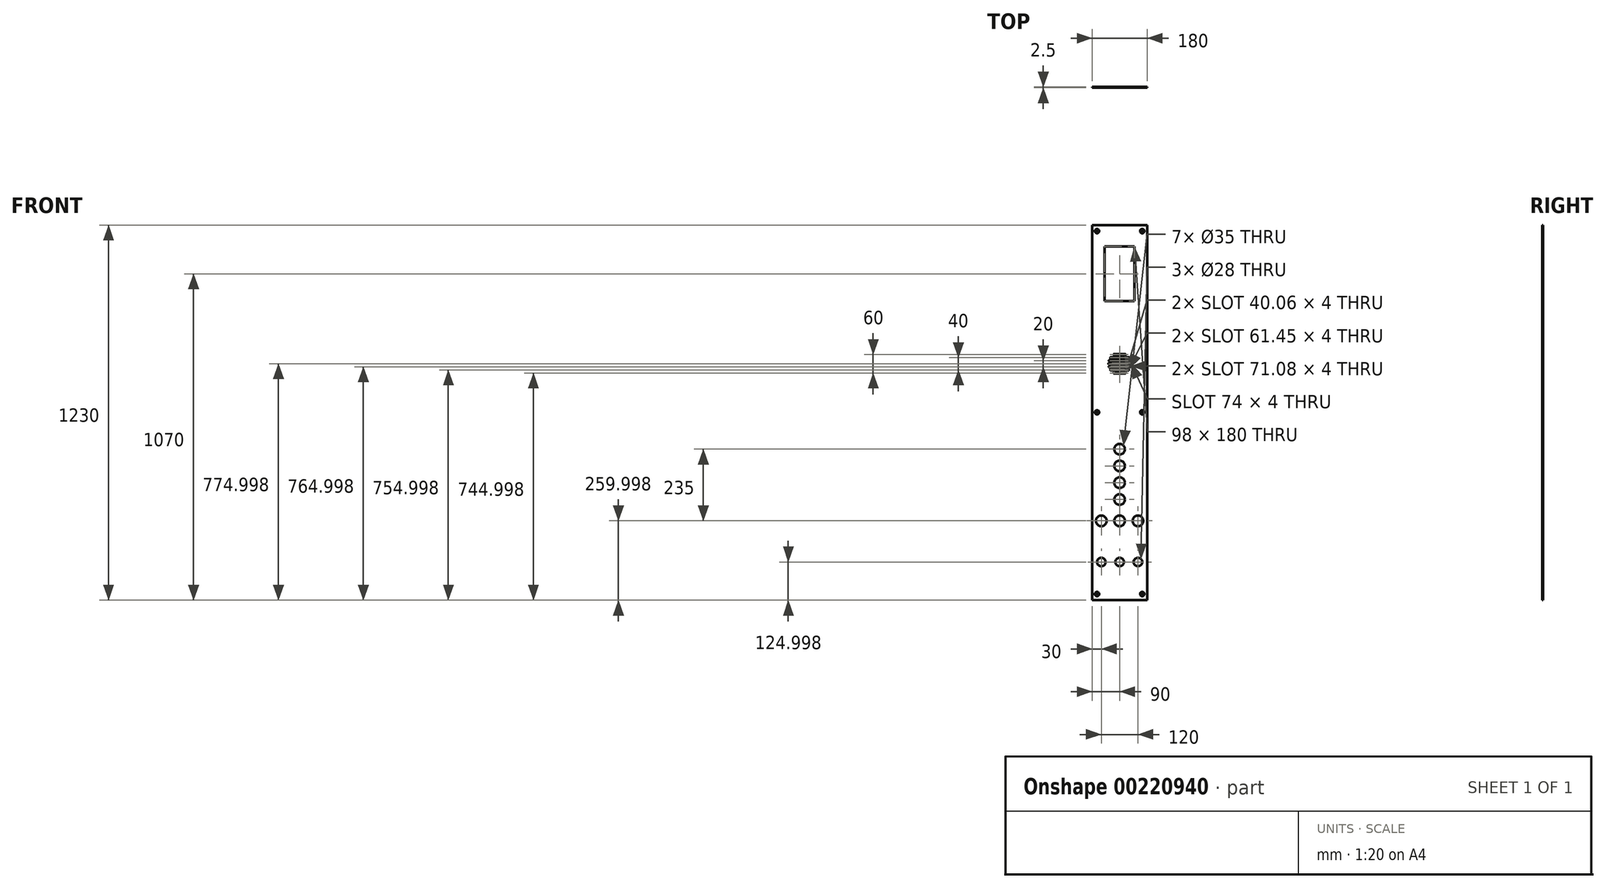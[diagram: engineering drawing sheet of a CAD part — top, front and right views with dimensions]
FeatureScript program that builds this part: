
annotation { "Feature Type Name" : "Feature", "Feature Type Description" : "" }
export const myFeature = defineFeature(function(context is Context, id is Id, definition is map)
    precondition{}
    {
        {
            var Q0;
            Q0=qCreatedBy(makeId("Front.planeOp"),FACE);
            var sketch = newSketch(context, id + "F0", { "sketchPlane" : qUnion([Q0])});
            skLineSegment(sketch, "E0.bottom", {"start": v(-139, 614.56) * mm, "end": v(41, 614.56) * mm});
            skLineSegment(sketch, "E0.top", {"start": v(-139, -615.44) * mm, "end": v(41, -615.44) * mm});
            skLineSegment(sketch, "E0.left", {"start": v(-139, 614.56) * mm, "end": v(-139, -615.44) * mm});
            skLineSegment(sketch, "E0.right", {"start": v(41, 614.56) * mm, "end": v(41, -615.44) * mm});
            skLineSegment(sketch, "E1.bottom", {"start": v(-98, 544.56) * mm, "end": v(0, 544.56) * mm});
            skLineSegment(sketch, "E1.top", {"start": v(-98, 364.56) * mm, "end": v(0, 364.56) * mm});
            skLineSegment(sketch, "E1.left", {"start": v(-98, 544.56) * mm, "end": v(-98, 364.56) * mm});
            skLineSegment(sketch, "E1.right", {"start": v(0, 544.56) * mm, "end": v(0, 364.56) * mm});
            skLineSegment(sketch, "E2", {"start": v(-49, 614.56) * mm, "end": v(-49, -615.44) * mm, "construction": true});
            skCircle(sketch, "E3", {"center": v(-49, -355.44) * mm, "radius": 17.5 * mm});
            skCircle(sketch, "E4", {"center": v(-49, -285.44) * mm, "radius": 17.5 * mm});
            skCircle(sketch, "E5", {"center": v(-49, -230.44) * mm, "radius": 17.5 * mm});
            skCircle(sketch, "E6", {"center": v(-49, -175.44) * mm, "radius": 17.5 * mm});
            skCircle(sketch, "E7", {"center": v(-49, -120.44) * mm, "radius": 17.5 * mm});
            skLineSegment(sketch, "E8", {"start": v(-49, -355.44) * mm, "end": v(-139, -355.44) * mm, "construction": true});
            skLineSegment(sketch, "E9", {"start": v(-49, -355.44) * mm, "end": v(41, -355.44) * mm, "construction": true});
            skCircle(sketch, "E10", {"center": v(-109, -355.44) * mm, "radius": 17.5 * mm});
            skCircle(sketch, "E11", {"center": v(11, -355.44) * mm, "radius": 17.5 * mm});
            skCircle(sketch, "E12", {"center": v(-49, 159.56) * mm, "radius": 35 * mm, "construction": true});
            skLineSegment(sketch, "E13", {"start": v(-84, 159.56) * mm, "end": v(-14, 159.56) * mm});
            skLineSegment(sketch, "E14.1.0.0", {"start": v(-82.54, 149.56) * mm, "end": v(-15.46, 149.56) * mm});
            skLineSegment(sketch, "E14.2.0.0", {"start": v(-77.72, 139.56) * mm, "end": v(-20.28, 139.56) * mm});
            skLineSegment(sketch, "E14.3.0.0", {"start": v(-67.03, 129.56) * mm, "end": v(-30.97, 129.56) * mm});
            skLineSegment(sketch, "E15.1.0.0", {"start": v(-82.54, 169.56) * mm, "end": v(-15.46, 169.56) * mm});
            skLineSegment(sketch, "E15.2.0.0", {"start": v(-77.72, 179.56) * mm, "end": v(-20.28, 179.56) * mm});
            skLineSegment(sketch, "E15.3.0.0", {"start": v(-67.03, 189.56) * mm, "end": v(-30.97, 189.56) * mm});
            skPoint(sketch, "E16.orphan", {"position": v(-84, 189.56) * mm});
            skPoint(sketch, "E17.orphan", {"position": v(-84, 179.56) * mm});
            skPoint(sketch, "E18.orphan", {"position": v(-14, 189.56) * mm});
            skPoint(sketch, "E19.orphan", {"position": v(-14, 179.56) * mm});
            skPoint(sketch, "E20.orphan", {"position": v(-14, 169.56) * mm});
            skPoint(sketch, "E21.orphan", {"position": v(-14, 149.56) * mm});
            skPoint(sketch, "E22.orphan", {"position": v(-14, 139.56) * mm});
            skPoint(sketch, "E23.orphan", {"position": v(-14, 129.56) * mm});
            skPoint(sketch, "E24.orphan", {"position": v(-84, 129.56) * mm});
            skPoint(sketch, "E25.orphan", {"position": v(-84, 139.56) * mm});
            skLineSegment(sketch, "E26.MirrorCS", {"start": v(-30.97, 189.56) * mm, "end": v(-67.03, 189.56) * mm});
            skArc(sketch, "E27.0.startCap", {"start": v(-67.03, 187.56) * mm, "mid": v(-69.03, 189.56) * mm, "end": v(-67.03, 191.56) * mm});
            skArc(sketch, "E27.0.endCap", {"start": v(-30.97, 191.56) * mm, "mid": v(-28.97, 189.56) * mm, "end": v(-30.97, 187.56) * mm});
            skLineSegment(sketch, "E27.0.left", {"start": v(-67.03, 191.56) * mm, "end": v(-30.97, 191.56) * mm});
            skLineSegment(sketch, "E27.0.right", {"start": v(-67.03, 187.56) * mm, "end": v(-30.97, 187.56) * mm});
            skArc(sketch, "E28.0.startCap", {"start": v(-77.72, 177.56) * mm, "mid": v(-79.72, 179.56) * mm, "end": v(-77.72, 181.56) * mm});
            skArc(sketch, "E28.0.endCap", {"start": v(-20.28, 181.56) * mm, "mid": v(-18.28, 179.56) * mm, "end": v(-20.28, 177.56) * mm});
            skLineSegment(sketch, "E28.0.left", {"start": v(-77.72, 181.56) * mm, "end": v(-20.28, 181.56) * mm});
            skLineSegment(sketch, "E28.0.right", {"start": v(-77.72, 177.56) * mm, "end": v(-20.28, 177.56) * mm});
            skArc(sketch, "E29.0.startCap", {"start": v(-82.54, 167.56) * mm, "mid": v(-84.54, 169.56) * mm, "end": v(-82.54, 171.56) * mm});
            skArc(sketch, "E29.0.endCap", {"start": v(-15.46, 171.56) * mm, "mid": v(-13.46, 169.56) * mm, "end": v(-15.46, 167.56) * mm});
            skLineSegment(sketch, "E29.0.left", {"start": v(-82.54, 171.56) * mm, "end": v(-15.46, 171.56) * mm});
            skLineSegment(sketch, "E29.0.right", {"start": v(-82.54, 167.56) * mm, "end": v(-15.46, 167.56) * mm});
            skArc(sketch, "E30.0.startCap", {"start": v(-84, 157.56) * mm, "mid": v(-86, 159.56) * mm, "end": v(-84, 161.56) * mm});
            skArc(sketch, "E30.0.endCap", {"start": v(-14, 161.56) * mm, "mid": v(-12, 159.56) * mm, "end": v(-14, 157.56) * mm});
            skLineSegment(sketch, "E30.0.left", {"start": v(-84, 161.56) * mm, "end": v(-14, 161.56) * mm});
            skLineSegment(sketch, "E30.0.right", {"start": v(-84, 157.56) * mm, "end": v(-14, 157.56) * mm});
            skArc(sketch, "E31.0.startCap", {"start": v(-82.54, 147.56) * mm, "mid": v(-84.54, 149.56) * mm, "end": v(-82.54, 151.56) * mm});
            skArc(sketch, "E31.0.endCap", {"start": v(-15.46, 151.56) * mm, "mid": v(-13.46, 149.56) * mm, "end": v(-15.46, 147.56) * mm});
            skLineSegment(sketch, "E31.0.left", {"start": v(-82.54, 151.56) * mm, "end": v(-15.46, 151.56) * mm});
            skLineSegment(sketch, "E31.0.right", {"start": v(-82.54, 147.56) * mm, "end": v(-15.46, 147.56) * mm});
            skArc(sketch, "E32.0.startCap", {"start": v(-77.72, 137.56) * mm, "mid": v(-79.72, 139.56) * mm, "end": v(-77.72, 141.56) * mm});
            skArc(sketch, "E32.0.endCap", {"start": v(-20.28, 141.56) * mm, "mid": v(-18.28, 139.56) * mm, "end": v(-20.28, 137.56) * mm});
            skLineSegment(sketch, "E32.0.left", {"start": v(-77.72, 141.56) * mm, "end": v(-20.28, 141.56) * mm});
            skLineSegment(sketch, "E32.0.right", {"start": v(-77.72, 137.56) * mm, "end": v(-20.28, 137.56) * mm});
            skArc(sketch, "E33.0.startCap", {"start": v(-67.03, 127.56) * mm, "mid": v(-69.03, 129.56) * mm, "end": v(-67.03, 131.56) * mm});
            skArc(sketch, "E33.0.endCap", {"start": v(-30.97, 131.56) * mm, "mid": v(-28.97, 129.56) * mm, "end": v(-30.97, 127.56) * mm});
            skLineSegment(sketch, "E33.0.left", {"start": v(-67.03, 131.56) * mm, "end": v(-30.97, 131.56) * mm});
            skLineSegment(sketch, "E33.0.right", {"start": v(-67.03, 127.56) * mm, "end": v(-30.97, 127.56) * mm});
            skCircle(sketch, "E34", {"center": v(-123, -595.44) * mm, "radius": 3 * mm});
            skCircle(sketch, "E35", {"center": v(-123, 594.56) * mm, "radius": 3 * mm});
            skCircle(sketch, "E36", {"center": v(-123, 0.56) * mm, "radius": 3 * mm});
            skCircle(sketch, "E37.MirrorC", {"center": v(25, 594.56) * mm, "radius": 3 * mm});
            skCircle(sketch, "E38.MirrorC", {"center": v(25, 0.56) * mm, "radius": 3 * mm});
            skCircle(sketch, "E39.MirrorC", {"center": v(25, -595.44) * mm, "radius": 3 * mm});
            skLineSegment(sketch, "E40", {"start": v(-139, -490.44) * mm, "end": v(41, -490.44) * mm, "construction": true});
            skCircle(sketch, "E41", {"center": v(-109, -490.44) * mm, "radius": 14 * mm});
            skCircle(sketch, "E42", {"center": v(-49, -490.44) * mm, "radius": 14 * mm});
            skCircle(sketch, "E43", {"center": v(11, -490.44) * mm, "radius": 14 * mm});
            skSolve(sketch);
        }
        {
            var Q0;
            Q0=makeQuery(id+"F0.imprint","IMPRINT",FACE,{"disambiguationData":[TD([[makeQuery(id+"F0.imprint","IMPRINT",EDGE,{"derivedFrom":sQuery(id+"F0.wireOp",EDGE,"E0.bottom")}),-1.0]])]});
            extrude(context, id + "F1", {"entities" : qUnion([Q0]), "depth" : 2.5 * mm});
        }
        {
            var Q0;
            Q0=makeQuery(id+"F1.opExtrude","CAP_EDGE",EDGE,{"disambiguationData":[OSD([sQuery(id+"F0.wireOp",EDGE,"E39.MirrorC")])],"isStart":false});
            var Q1;
            Q1=makeQuery(id+"F1.opExtrude","CAP_EDGE",EDGE,{"disambiguationData":[OSD([sQuery(id+"F0.wireOp",EDGE,"E34")])],"isStart":false});
            var Q2;
            Q2=makeQuery(id+"F1.opExtrude","CAP_EDGE",EDGE,{"disambiguationData":[OSD([sQuery(id+"F0.wireOp",EDGE,"E36")])],"isStart":false});
            var Q3;
            Q3=makeQuery(id+"F1.opExtrude","CAP_EDGE",EDGE,{"disambiguationData":[OSD([sQuery(id+"F0.wireOp",EDGE,"E38.MirrorC")])],"isStart":false});
            var Q4;
            Q4=makeQuery(id+"F1.opExtrude","CAP_EDGE",EDGE,{"disambiguationData":[OSD([sQuery(id+"F0.wireOp",EDGE,"E37.MirrorC")])],"isStart":false});
            var Q5;
            Q5=makeQuery(id+"F1.opExtrude","CAP_EDGE",EDGE,{"disambiguationData":[OSD([sQuery(id+"F0.wireOp",EDGE,"E35")])],"isStart":false});
            chamfer(context, id + "F2", {"entities" : qUnion([Q0, Q1, Q2, Q3, Q4, Q5]), "chamferType" : ChamferType.OFFSET_ANGLE, "width" : 4 * mm, "oppositeDirection" : false, "angle" : 45 * degree, "tangentPropagation" : true});
        }
        {
            var Q0;
            Q0=makeQuery(id+"F1.opExtrude","CAP_FACE",FACE,{"disambiguationData":[OSD([sQuery(id+"F0.wireOp",EDGE,"E0.bottom"),sQuery(id+"F0.wireOp",EDGE,"E0.top"),sQuery(id+"F0.wireOp",EDGE,"E0.left"),sQuery(id+"F0.wireOp",EDGE,"E0.right"),sQuery(id+"F0.wireOp",EDGE,"E1.bottom"),sQuery(id+"F0.wireOp",EDGE,"E1.top"),sQuery(id+"F0.wireOp",EDGE,"E1.left"),sQuery(id+"F0.wireOp",EDGE,"E1.right"),sQuery(id+"F0.wireOp",EDGE,"E3"),sQuery(id+"F0.wireOp",EDGE,"E4"),sQuery(id+"F0.wireOp",EDGE,"E5"),sQuery(id+"F0.wireOp",EDGE,"E6"),sQuery(id+"F0.wireOp",EDGE,"E7"),sQuery(id+"F0.wireOp",EDGE,"E10"),sQuery(id+"F0.wireOp",EDGE,"E11"),sQuery(id+"F0.wireOp",EDGE,"E27.0.startCap"),sQuery(id+"F0.wireOp",EDGE,"E27.0.endCap"),sQuery(id+"F0.wireOp",EDGE,"E27.0.left"),sQuery(id+"F0.wireOp",EDGE,"E27.0.right"),sQuery(id+"F0.wireOp",EDGE,"E28.0.startCap"),sQuery(id+"F0.wireOp",EDGE,"E28.0.endCap"),sQuery(id+"F0.wireOp",EDGE,"E28.0.left"),sQuery(id+"F0.wireOp",EDGE,"E28.0.right"),sQuery(id+"F0.wireOp",EDGE,"E29.0.startCap"),sQuery(id+"F0.wireOp",EDGE,"E29.0.endCap"),sQuery(id+"F0.wireOp",EDGE,"E29.0.left"),sQuery(id+"F0.wireOp",EDGE,"E29.0.right"),sQuery(id+"F0.wireOp",EDGE,"E30.0.startCap"),sQuery(id+"F0.wireOp",EDGE,"E30.0.endCap"),sQuery(id+"F0.wireOp",EDGE,"E30.0.left"),sQuery(id+"F0.wireOp",EDGE,"E30.0.right"),sQuery(id+"F0.wireOp",EDGE,"E31.0.startCap"),sQuery(id+"F0.wireOp",EDGE,"E31.0.endCap"),sQuery(id+"F0.wireOp",EDGE,"E31.0.left"),sQuery(id+"F0.wireOp",EDGE,"E31.0.right"),sQuery(id+"F0.wireOp",EDGE,"E32.0.startCap"),sQuery(id+"F0.wireOp",EDGE,"E32.0.endCap"),sQuery(id+"F0.wireOp",EDGE,"E32.0.left"),sQuery(id+"F0.wireOp",EDGE,"E32.0.right"),sQuery(id+"F0.wireOp",EDGE,"E33.0.startCap"),sQuery(id+"F0.wireOp",EDGE,"E33.0.endCap"),sQuery(id+"F0.wireOp",EDGE,"E33.0.left"),sQuery(id+"F0.wireOp",EDGE,"E33.0.right"),sQuery(id+"F0.wireOp",EDGE,"E34"),sQuery(id+"F0.wireOp",EDGE,"E35"),sQuery(id+"F0.wireOp",EDGE,"E36"),sQuery(id+"F0.wireOp",EDGE,"E37.MirrorC"),sQuery(id+"F0.wireOp",EDGE,"E38.MirrorC"),sQuery(id+"F0.wireOp",EDGE,"E39.MirrorC"),sQuery(id+"F0.wireOp",EDGE,"E41"),sQuery(id+"F0.wireOp",EDGE,"E42"),sQuery(id+"F0.wireOp",EDGE,"E43")])],"isStart":true});
            var sketch = newSketch(context, id + "F3", { "sketchPlane" : qUnion([Q0])});
            skCircle(sketch, "E44", {"center": v(-23.57, 511.56) * mm, "radius": 2 * mm});
            skCircle(sketch, "E45", {"center": v(-22, 396.56) * mm, "radius": 2 * mm});
            skLineSegment(sketch, "E46", {"start": v(49, 614.56) * mm, "end": v(49, -615.44) * mm, "construction": true});
            skLineSegment(sketch, "E47", {"start": v(-22, 396.56) * mm, "end": v(-23.57, 511.56) * mm, "construction": true});
            skCircle(sketch, "E48.MirrorC", {"center": v(120, 396.56) * mm, "radius": 2 * mm});
            skCircle(sketch, "E49.MirrorC", {"center": v(121.57, 511.56) * mm, "radius": 2 * mm});
            skLineSegment(sketch, "E50.MirrorCS", {"start": v(120, 396.56) * mm, "end": v(121.57, 511.56) * mm, "construction": true});
            skLineSegment(sketch, "E51", {"start": v(49, -120.44) * mm, "end": v(-41, -120.44) * mm, "construction": true});
            skLineSegment(sketch, "E52", {"start": v(49, -175.44) * mm, "end": v(-41, -175.44) * mm, "construction": true});
            skLineSegment(sketch, "E53", {"start": v(49, -230.44) * mm, "end": v(-41, -230.44) * mm, "construction": true});
            skLineSegment(sketch, "E54", {"start": v(49, -285.44) * mm, "end": v(-41, -285.44) * mm, "construction": true});
            skLineSegment(sketch, "E55", {"start": v(49, -355.44) * mm, "end": v(-41, -355.44) * mm, "construction": true});
            skCircle(sketch, "E56", {"center": v(23.6, -230.44) * mm, "radius": 2 * mm});
            skCircle(sketch, "E57", {"center": v(23.6, -285.44) * mm, "radius": 2 * mm});
            skPoint(sketch, "E57.centerSnap0", {"position": v(4, -285.44) * mm});
            skCircle(sketch, "E58", {"center": v(23.6, -355.44) * mm, "radius": 2 * mm});
            skCircle(sketch, "E59", {"center": v(23.6, -175.44) * mm, "radius": 2 * mm});
            skCircle(sketch, "E60", {"center": v(23.6, -120.44) * mm, "radius": 2 * mm});
            skCircle(sketch, "E61", {"center": v(14.4, -355.44) * mm, "radius": 2 * mm});
            skCircle(sketch, "E62", {"center": v(-36.4, -355.44) * mm, "radius": 2 * mm});
            skCircle(sketch, "E63.MirrorC", {"center": v(74.4, -120.44) * mm, "radius": 2 * mm});
            skCircle(sketch, "E64.MirrorC", {"center": v(74.4, -175.44) * mm, "radius": 2 * mm});
            skCircle(sketch, "E65.MirrorC", {"center": v(74.4, -230.44) * mm, "radius": 2 * mm});
            skCircle(sketch, "E66.MirrorC", {"center": v(74.4, -285.44) * mm, "radius": 2 * mm});
            skCircle(sketch, "E67.MirrorC", {"center": v(74.4, -355.44) * mm, "radius": 2 * mm});
            skCircle(sketch, "E68.MirrorC", {"center": v(83.6, -355.44) * mm, "radius": 2 * mm});
            skCircle(sketch, "E69.MirrorC", {"center": v(134.4, -355.44) * mm, "radius": 2 * mm});
            skCircle(sketch, "E70", {"center": v(-7, -557.44) * mm, "radius": 2 * mm});
            skCircle(sketch, "E71", {"center": v(-7, -543.44) * mm, "radius": 2 * mm});
            skCircle(sketch, "E72", {"center": v(-7, 288.56) * mm, "radius": 2 * mm});
            skCircle(sketch, "E73", {"center": v(-7, 274.56) * mm, "radius": 2 * mm});
            skSolve(sketch);
        }
        {
            var Q0;
            Q0=sQuery(id+"F3.wireOp",EDGE,"E62");
            var Q1;
            Q1=sQuery(id+"F3.wireOp",EDGE,"E61");
            var Q2;
            Q2=sQuery(id+"F3.wireOp",EDGE,"E58");
            var Q3;
            Q3=sQuery(id+"F3.wireOp",EDGE,"E67.MirrorC");
            var Q4;
            Q4=sQuery(id+"F3.wireOp",EDGE,"E68.MirrorC");
            var Q5;
            Q5=sQuery(id+"F3.wireOp",EDGE,"E69.MirrorC");
            var Q6;
            Q6=sQuery(id+"F3.wireOp",EDGE,"E66.MirrorC");
            var Q7;
            Q7=sQuery(id+"F3.wireOp",EDGE,"E57");
            var Q8;
            Q8=sQuery(id+"F3.wireOp",EDGE,"E65.MirrorC");
            var Q9;
            Q9=sQuery(id+"F3.wireOp",EDGE,"E56");
            var Q10;
            Q10=sQuery(id+"F3.wireOp",EDGE,"E64.MirrorC");
            var Q11;
            Q11=sQuery(id+"F3.wireOp",EDGE,"E59");
            var Q12;
            Q12=sQuery(id+"F3.wireOp",EDGE,"E60");
            var Q13;
            Q13=sQuery(id+"F3.wireOp",EDGE,"E63.MirrorC");
            var Q14;
            Q14=sQuery(id+"F3.wireOp",EDGE,"E48.MirrorC");
            var Q15;
            Q15=sQuery(id+"F3.wireOp",EDGE,"E49.MirrorC");
            var Q16;
            Q16=sQuery(id+"F3.wireOp",EDGE,"E44");
            var Q17;
            Q17=sQuery(id+"F3.wireOp",EDGE,"E45");
            extrude(context, id + "F4", {"bodyType" : ToolBodyType.SURFACE, "surfaceEntities" : qUnion([Q0, Q1, Q2, Q3, Q4, Q5, Q6, Q7, Q8, Q9, Q10, Q11, Q12, Q13, Q14, Q15, Q16, Q17]), "depth" : 25 * mm});
        }
        {
            var Q0;
            Q0=sQuery(id+"F3.wireOp",EDGE,"E72");
            var Q1;
            Q1=sQuery(id+"F3.wireOp",EDGE,"E73");
            extrude(context, id + "F5", {"bodyType" : ToolBodyType.SURFACE, "surfaceEntities" : qUnion([Q0, Q1]), "depth" : 25 * mm});
        }
        {
            var Q0;
            Q0=sQuery(id+"F3.wireOp",EDGE,"E71");
            var Q1;
            Q1=sQuery(id+"F3.wireOp",EDGE,"E70");
            extrude(context, id + "F6", {"bodyType" : ToolBodyType.SURFACE, "surfaceEntities" : qUnion([Q0, Q1]), "depth" : 25 * mm});
        }
    });
